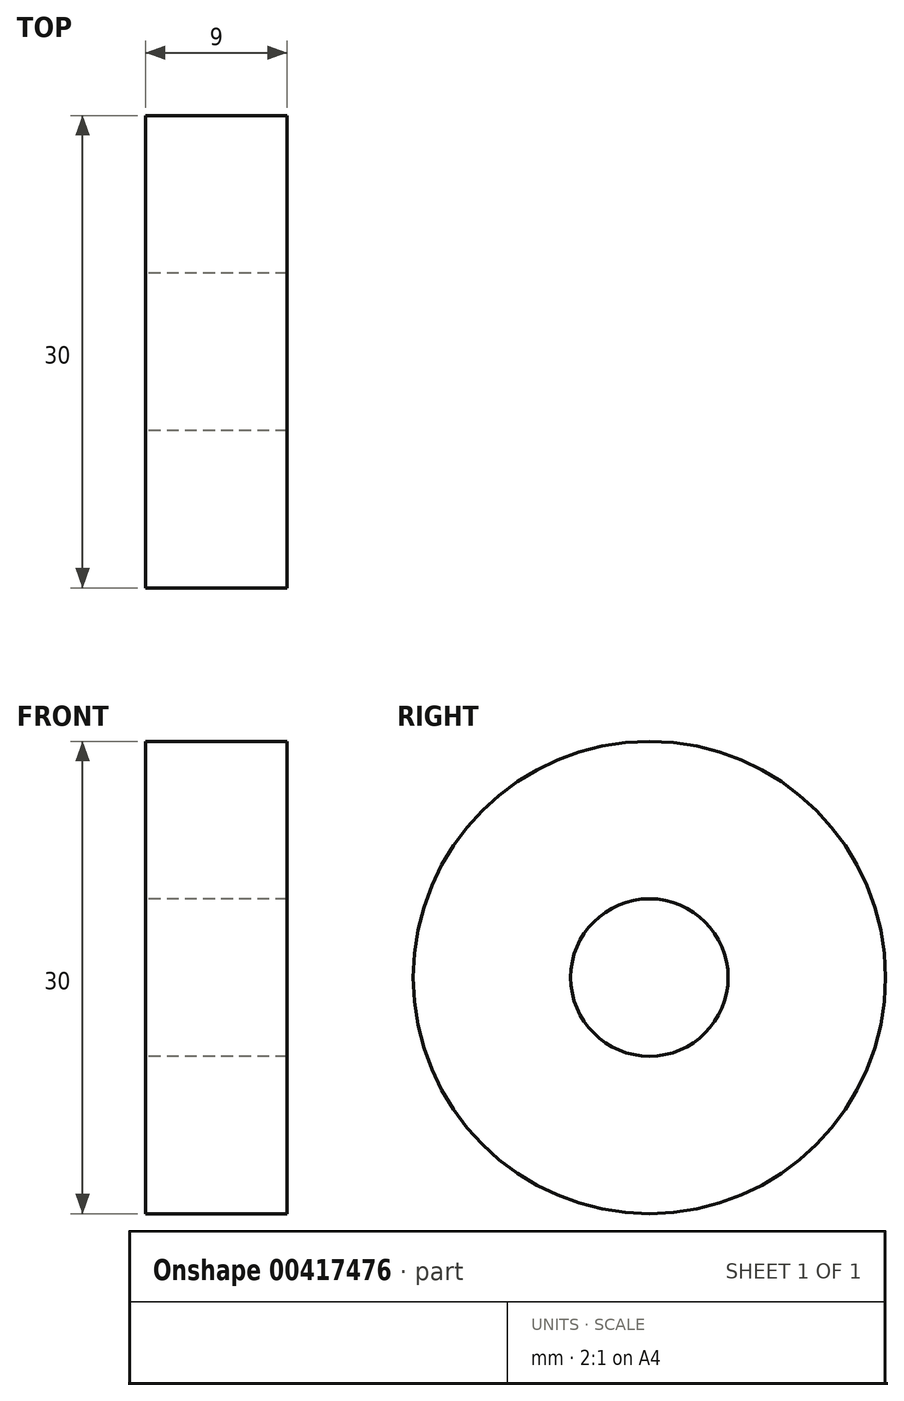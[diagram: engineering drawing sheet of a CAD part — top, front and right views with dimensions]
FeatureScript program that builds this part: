
annotation { "Feature Type Name" : "Feature", "Feature Type Description" : "" }
export const myFeature = defineFeature(function(context is Context, id is Id, definition is map)
    precondition{}
    {
        {
            var Q0;
            Q0=qCreatedBy(makeId("Right.planeOp"),FACE);
            var sketch = newSketch(context, id + "F0", { "sketchPlane" : qUnion([Q0])});
            skCircle(sketch, "E0", {"center": v(0, 0) * mm, "radius": 15 * mm});
            skCircle(sketch, "E1", {"center": v(0, 0) * mm, "radius": 5 * mm});
            skSolve(sketch);
        }
        {
            var Q0;
            Q0=makeQuery(id+"F0.imprint","IMPRINT",FACE,{"disambiguationData":[TD([[makeQuery(id+"F0.imprint","IMPRINT",EDGE,{"derivedFrom":sQuery(id+"F0.wireOp",EDGE,"E0")}),1.0]])]});
            extrude(context, id + "F1", {"entities" : qUnion([Q0]), "depth" : 9 * mm});
        }
    });
